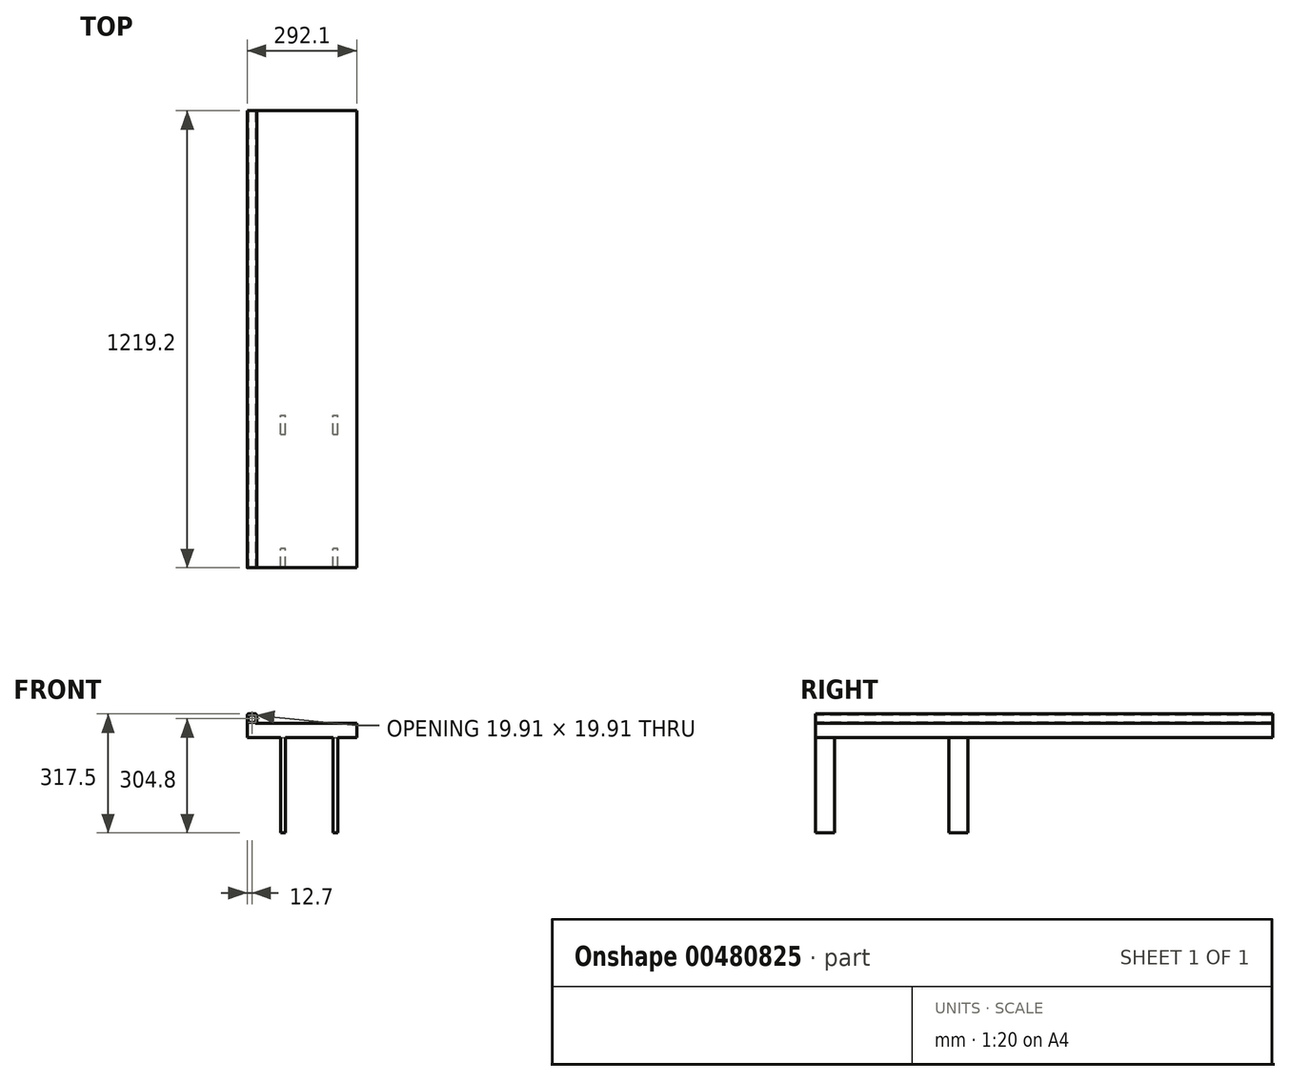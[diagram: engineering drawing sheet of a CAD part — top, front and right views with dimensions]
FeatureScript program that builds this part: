
annotation { "Feature Type Name" : "Feature", "Feature Type Description" : "" }
export const myFeature = defineFeature(function(context is Context, id is Id, definition is map)
    precondition{}
    {
        {
            var Q0;
            Q0=qCreatedBy(makeId("Front.planeOp"),FACE);
            var sketch = newSketch(context, id + "F0", { "sketchPlane" : qUnion([Q0])});
            skLineSegment(sketch, "E0.bottom", {"start": v(0, 0) * mm, "end": v(292.1, 0) * mm});
            skLineSegment(sketch, "E0.top", {"start": v(0, 38.1) * mm, "end": v(292.1, 38.1) * mm});
            skLineSegment(sketch, "E0.left", {"start": v(0, 0) * mm, "end": v(0, 38.1) * mm});
            skLineSegment(sketch, "E0.right", {"start": v(292.1, 0) * mm, "end": v(292.1, 38.1) * mm});
            skSolve(sketch);
        }
        {
            var Q0;
            Q0 = qSketchRegion(id + "F0", true);
            extrude(context, id + "F1", {"entities" : qUnion([Q0]), "depth" : 1219.2 * mm});
        }
        {
            var Q0;
            Q0=makeQuery(id+"F1.opExtrude","CAP_FACE",FACE,{"disambiguationData":[OSD([sQuery(id+"F0.wireOp",EDGE,"E0.bottom"),sQuery(id+"F0.wireOp",EDGE,"E0.top"),sQuery(id+"F0.wireOp",EDGE,"E0.left"),sQuery(id+"F0.wireOp",EDGE,"E0.right")])],"isStart":false});
            var sketch = newSketch(context, id + "F2", { "sketchPlane" : qUnion([Q0])});
            skLineSegment(sketch, "E1.bottom", {"start": v(3.17, 38.1) * mm, "end": v(22.23, 38.1) * mm});
            skLineSegment(sketch, "E1.top", {"start": v(3.17, 63.5) * mm, "end": v(22.22, 63.5) * mm});
            skLineSegment(sketch, "E1.left", {"start": v(0, 41.27) * mm, "end": v(0, 60.33) * mm});
            skLineSegment(sketch, "E1.right", {"start": v(25.4, 41.27) * mm, "end": v(25.4, 60.33) * mm});
            skPoint(sketch, "E2.visualSharp", {"position": v(25.4, 63.5) * mm});
            skArc(sketch, "E2.filletArc", {"start": v(25.4, 60.33) * mm, "mid": v(24.47, 62.57) * mm, "end": v(22.22, 63.5) * mm});
            skPoint(sketch, "E3.visualSharp", {"position": v(0, 63.5) * mm});
            skArc(sketch, "E3.filletArc", {"start": v(3.17, 63.5) * mm, "mid": v(0.93, 62.57) * mm, "end": v(0, 60.33) * mm});
            skPoint(sketch, "E4.visualSharp", {"position": v(0, 38.1) * mm});
            skArc(sketch, "E4.filletArc", {"start": v(0, 41.27) * mm, "mid": v(0.93, 39.03) * mm, "end": v(3.17, 38.1) * mm});
            skPoint(sketch, "E5.visualSharp", {"position": v(25.4, 38.1) * mm});
            skArc(sketch, "E5.filletArc", {"start": v(22.23, 38.1) * mm, "mid": v(24.47, 39.03) * mm, "end": v(25.4, 41.27) * mm});
            skArc(sketch, "E6.0", {"start": v(22.23, 40.84) * mm, "mid": v(22.53, 40.97) * mm, "end": v(22.66, 41.27) * mm});
            skLineSegment(sketch, "E6.1", {"start": v(3.17, 40.84) * mm, "end": v(22.23, 40.84) * mm});
            skLineSegment(sketch, "E6.2", {"start": v(22.66, 41.27) * mm, "end": v(22.66, 60.33) * mm});
            skArc(sketch, "E6.3", {"start": v(2.74, 41.27) * mm, "mid": v(2.87, 40.97) * mm, "end": v(3.17, 40.84) * mm});
            skArc(sketch, "E6.4", {"start": v(22.66, 60.33) * mm, "mid": v(22.53, 60.63) * mm, "end": v(22.22, 60.76) * mm});
            skLineSegment(sketch, "E6.5", {"start": v(3.17, 60.76) * mm, "end": v(22.22, 60.76) * mm});
            skArc(sketch, "E6.6", {"start": v(3.17, 60.76) * mm, "mid": v(2.87, 60.63) * mm, "end": v(2.74, 60.33) * mm});
            skLineSegment(sketch, "E6.7", {"start": v(2.74, 41.27) * mm, "end": v(2.74, 60.33) * mm});
            skSolve(sketch);
        }
        {
            var Q0;
            Q0 = qSketchRegion(id + "F2", true);
            extrude(context, id + "F3", {"entities" : qUnion([Q0]), "operationType" : NewBodyOperationType.ADD, "oppositeDirection" : true, "depth" : 1219.2 * mm});
        }
        {
            var Q0;
            Q0=makeQuery(id+"F1.opExtrude","SWEPT_FACE",FACE,{"disambiguationData":[OSD([sQuery(id+"F0.wireOp",EDGE,"E0.bottom")])]});
            var sketch = newSketch(context, id + "F4", { "sketchPlane" : qUnion([Q0])});
            skLineSegment(sketch, "E7.bottom", {"start": v(101.6, 1219.2) * mm, "end": v(88.9, 1219.2) * mm});
            skLineSegment(sketch, "E7.top", {"start": v(101.6, 1168.4) * mm, "end": v(88.9, 1168.4) * mm});
            skLineSegment(sketch, "E7.left", {"start": v(101.6, 1219.2) * mm, "end": v(101.6, 1168.4) * mm});
            skLineSegment(sketch, "E7.right", {"start": v(88.9, 1219.2) * mm, "end": v(88.9, 1168.4) * mm});
            skLineSegment(sketch, "E8.bottom", {"start": v(241.3, 1219.2) * mm, "end": v(228.6, 1219.2) * mm});
            skLineSegment(sketch, "E8.top", {"start": v(241.3, 1168.4) * mm, "end": v(228.6, 1168.4) * mm});
            skLineSegment(sketch, "E8.left", {"start": v(241.3, 1219.2) * mm, "end": v(241.3, 1168.4) * mm});
            skLineSegment(sketch, "E8.right", {"start": v(228.6, 1219.2) * mm, "end": v(228.6, 1168.4) * mm});
            skLineSegment(sketch, "E9.bottom", {"start": v(88.9, 863.6) * mm, "end": v(101.6, 863.6) * mm});
            skLineSegment(sketch, "E9.top", {"start": v(88.9, 812.8) * mm, "end": v(101.6, 812.8) * mm});
            skLineSegment(sketch, "E9.left", {"start": v(88.9, 863.6) * mm, "end": v(88.9, 812.8) * mm});
            skLineSegment(sketch, "E9.right", {"start": v(101.6, 863.6) * mm, "end": v(101.6, 812.8) * mm});
            skLineSegment(sketch, "E10.bottom", {"start": v(228.6, 863.6) * mm, "end": v(241.3, 863.6) * mm});
            skLineSegment(sketch, "E10.top", {"start": v(228.6, 812.8) * mm, "end": v(241.3, 812.8) * mm});
            skLineSegment(sketch, "E10.left", {"start": v(228.6, 863.6) * mm, "end": v(228.6, 812.8) * mm});
            skLineSegment(sketch, "E10.right", {"start": v(241.3, 863.6) * mm, "end": v(241.3, 812.8) * mm});
            skLineSegment(sketch, "E11", {"start": v(0, 1195.53) * mm, "end": v(88.9, 1195.53) * mm, "construction": true});
            skLineSegment(sketch, "E12", {"start": v(0, 1001.63) * mm, "end": v(88.9, 1001.63) * mm, "construction": true});
            skSolve(sketch);
        }
        {
            var Q0;
            Q0 = qSketchRegion(id + "F4", true);
            extrude(context, id + "F5", {"entities" : qUnion([Q0]), "operationType" : NewBodyOperationType.ADD, "depth" : 254 * mm});
        }
    });
